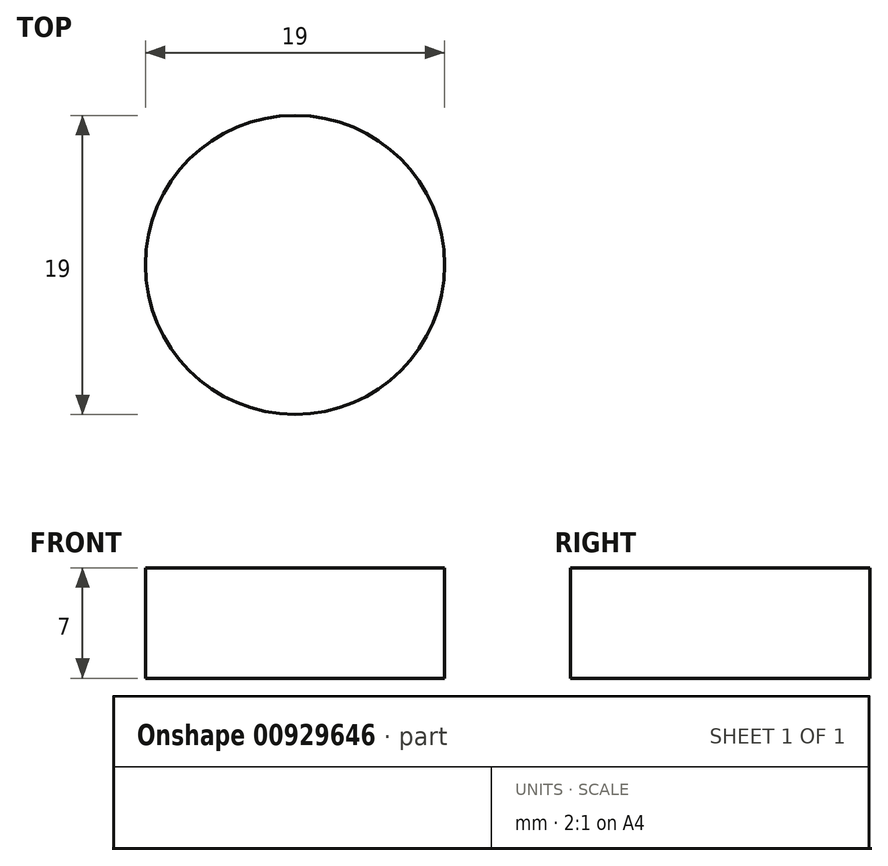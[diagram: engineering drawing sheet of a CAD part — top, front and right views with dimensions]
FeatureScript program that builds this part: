
annotation { "Feature Type Name" : "Feature", "Feature Type Description" : "" }
export const myFeature = defineFeature(function(context is Context, id is Id, definition is map)
    precondition{}
    {
        {
            var Q0;
            Q0=qCreatedBy(makeId("Top.planeOp"),FACE);
            var sketch = newSketch(context, id + "F0", { "sketchPlane" : qUnion([Q0])});
            skLineSegment(sketch, "E0.bottom", {"start": v(-40, 15) * mm, "end": v(40, 15) * mm});
            skLineSegment(sketch, "E0.top", {"start": v(-40, -15) * mm, "end": v(40, -15) * mm});
            skLineSegment(sketch, "E0.left", {"start": v(-40, 15) * mm, "end": v(-40, -15) * mm});
            skLineSegment(sketch, "E0.right", {"start": v(40, 15) * mm, "end": v(40, -15) * mm});
            skPoint(sketch, "E0.middle", {"position": v(0, 0) * mm});
            skSolve(sketch);
        }
        {
            var Q0;
            Q0 = qSketchRegion(id + "F0", true);
            extrude(context, id + "F1", {"entities" : qUnion([Q0]), "depth" : 7 * mm, "offsetDistance" : 25 * mm});
        }
        {
            var Q0;
            Q0=makeQuery(id+"F1.opExtrude","CAP_FACE",FACE,{"disambiguationData":[OSD([sQuery(id+"F0.wireOp",EDGE,"E0.bottom"),sQuery(id+"F0.wireOp",EDGE,"E0.top"),sQuery(id+"F0.wireOp",EDGE,"E0.left"),sQuery(id+"F0.wireOp",EDGE,"E0.right")])],"isStart":false});
            var sketch = newSketch(context, id + "F2", { "sketchPlane" : qUnion([Q0])});
            skCircle(sketch, "E1", {"center": v(0, 0) * mm, "radius": 11 * mm});
            skSolve(sketch);
        }
        {
            var Q0;
            Q0=makeQuery(id+"F2.imprint","IMPRINT",FACE,{"disambiguationData":[TD([[makeQuery(id+"F2.imprint","IMPRINT",EDGE,{"derivedFrom":sQuery(id+"F2.wireOp",EDGE,"E1")}),1.0]])]});
            extrude(context, id + "F3", {"entities" : qUnion([Q0]), "operationType" : NewBodyOperationType.REMOVE, "endBound" : BoundingType.THROUGH_ALL, "oppositeDirection" : true, "depth" : 25 * mm, "offsetDistance" : 25 * mm});
        }
        {
            var Q0;
            Q0=makeQuery(id+"F1.opExtrude","SWEPT_EDGE",EDGE,{"disambiguationData":[OSD([sQuery(id+"F0.wireOp",EDGE,"E0.bottom"),sQuery(id+"F0.wireOp",EDGE,"E0.left")])]});
            var Q1;
            Q1=makeQuery(id+"F1.opExtrude","SWEPT_EDGE",EDGE,{"disambiguationData":[OSD([sQuery(id+"F0.wireOp",EDGE,"E0.top"),sQuery(id+"F0.wireOp",EDGE,"E0.right")])]});
            var Q2;
            Q2=makeQuery(id+"F1.opExtrude","SWEPT_EDGE",EDGE,{"disambiguationData":[OSD([sQuery(id+"F0.wireOp",EDGE,"E0.bottom"),sQuery(id+"F0.wireOp",EDGE,"E0.right")])]});
            var Q3;
            Q3=makeQuery(id+"F1.opExtrude","SWEPT_EDGE",EDGE,{"disambiguationData":[OSD([sQuery(id+"F0.wireOp",EDGE,"E0.top"),sQuery(id+"F0.wireOp",EDGE,"E0.left")])]});
            chamfer(context, id + "F4", {"entities" : qUnion([Q0, Q1, Q2, Q3]), "width" : 10 * mm, "tangentPropagation" : true});
        }
        {
            var Q0;
            {var subQ0=sQuery(id+"F0.wireOp",EDGE,"E0.bottom");Q0=makeQuery(id+"F4.opChamfer","BLEND_EDGE",EDGE,{"blendedFrom":[makeQuery(id+"F1.opExtrude","SWEPT_EDGE",EDGE,{"disambiguationData":[OSD([subQ0,sQuery(id+"F0.wireOp",EDGE,"E0.left")])]}),makeQuery(id+"F1.opExtrude","SWEPT_FACE",FACE,{"disambiguationData":[OSD([subQ0])]})],"blendedInto":[makeQuery(id+"F1.opExtrude","SWEPT_FACE",FACE,{"disambiguationData":[OSD([subQ0])]})]});}
            var Q1;
            {var subQ0=sQuery(id+"F0.wireOp",EDGE,"E0.top");Q1=makeQuery(id+"F4.opChamfer","BLEND_EDGE",EDGE,{"blendedFrom":[makeQuery(id+"F1.opExtrude","SWEPT_EDGE",EDGE,{"disambiguationData":[OSD([subQ0,sQuery(id+"F0.wireOp",EDGE,"E0.left")])]}),makeQuery(id+"F1.opExtrude","SWEPT_FACE",FACE,{"disambiguationData":[OSD([subQ0])]})],"blendedInto":[makeQuery(id+"F1.opExtrude","SWEPT_FACE",FACE,{"disambiguationData":[OSD([subQ0])]})]});}
            var Q2;
            {var subQ0=sQuery(id+"F0.wireOp",EDGE,"E0.top");Q2=makeQuery(id+"F4.opChamfer","BLEND_EDGE",EDGE,{"blendedFrom":[makeQuery(id+"F1.opExtrude","SWEPT_EDGE",EDGE,{"disambiguationData":[OSD([subQ0,sQuery(id+"F0.wireOp",EDGE,"E0.right")])]}),makeQuery(id+"F1.opExtrude","SWEPT_FACE",FACE,{"disambiguationData":[OSD([subQ0])]})],"blendedInto":[makeQuery(id+"F1.opExtrude","SWEPT_FACE",FACE,{"disambiguationData":[OSD([subQ0])]})]});}
            var Q3;
            {var subQ0=sQuery(id+"F0.wireOp",EDGE,"E0.bottom");Q3=makeQuery(id+"F4.opChamfer","BLEND_EDGE",EDGE,{"blendedFrom":[makeQuery(id+"F1.opExtrude","SWEPT_EDGE",EDGE,{"disambiguationData":[OSD([subQ0,sQuery(id+"F0.wireOp",EDGE,"E0.right")])]}),makeQuery(id+"F1.opExtrude","SWEPT_FACE",FACE,{"disambiguationData":[OSD([subQ0])]})],"blendedInto":[makeQuery(id+"F1.opExtrude","SWEPT_FACE",FACE,{"disambiguationData":[OSD([subQ0])]})]});}
            fillet(context, id + "F5", {"entities" : qUnion([Q0, Q1, Q2, Q3]), "radius" : 5 * mm, "tangentPropagation" : true, "allowEdgeOverflow" : false});
        }
        {
            var Q0;
            Q0=makeQuery(id+"F1.opExtrude","CAP_FACE",FACE,{"disambiguationData":[OSD([sQuery(id+"F0.wireOp",EDGE,"E0.bottom"),sQuery(id+"F0.wireOp",EDGE,"E0.top"),sQuery(id+"F0.wireOp",EDGE,"E0.left"),sQuery(id+"F0.wireOp",EDGE,"E0.right")])],"isStart":false});
            var sketch = newSketch(context, id + "F6", { "sketchPlane" : qUnion([Q0])});
            skLineSegment(sketch, "E2", {"start": v(-29.84, 14.62) * mm, "end": v(-29.84, 0) * mm, "construction": true});
            skCircle(sketch, "E3", {"center": v(-29.84, 0) * mm, "radius": 9.5 * mm});
            skLineSegment(sketch, "E4", {"start": v(0, 15) * mm, "end": v(0, -15) * mm, "construction": true});
            skCircle(sketch, "E5.MirrorC", {"center": v(29.84, 0) * mm, "radius": 9.5 * mm});
            skSolve(sketch);
        }
        {
            var Q0;
            Q0=makeQuery(id+"F6.imprint","IMPRINT",FACE,{"disambiguationData":[TD([[makeQuery(id+"F6.imprint","IMPRINT",EDGE,{"derivedFrom":sQuery(id+"F6.wireOp",EDGE,"E5.MirrorC")}),-1.0]])]});
            var Q1;
            Q1=makeQuery(id+"F6.imprint","IMPRINT",FACE,{"disambiguationData":[TD([[makeQuery(id+"F6.imprint","IMPRINT",EDGE,{"derivedFrom":sQuery(id+"F6.wireOp",EDGE,"E3")}),1.0]])]});
            extrude(context, id + "F7", {"entities" : qUnion([Q0, Q1]), "operationType" : NewBodyOperationType.REMOVE, "endBound" : BoundingType.THROUGH_ALL, "oppositeDirection" : true, "depth" : 25 * mm, "offsetDistance" : 25 * mm});
        }
        {
            var Q0;
            Q0=makeQuery(id+"F1.opExtrude","CAP_FACE",FACE,{"disambiguationData":[OSD([sQuery(id+"F0.wireOp",EDGE,"E0.bottom"),sQuery(id+"F0.wireOp",EDGE,"E0.top"),sQuery(id+"F0.wireOp",EDGE,"E0.left"),sQuery(id+"F0.wireOp",EDGE,"E0.right")])],"isStart":false});
            var sketch = newSketch(context, id + "F8", { "sketchPlane" : qUnion([Q0])});
            skLineSegment(sketch, "E6", {"start": v(-17.7, 15) * mm, "end": v(-17.7, -15) * mm});
            skLineSegment(sketch, "E7", {"start": v(-17.7, -15) * mm, "end": v(-15.7, -15) * mm});
            skLineSegment(sketch, "E8", {"start": v(-15.7, -15) * mm, "end": v(-15.7, 15) * mm});
            skLineSegment(sketch, "E9", {"start": v(-15.7, 15) * mm, "end": v(-17.7, 15) * mm});
            skLineSegment(sketch, "E10", {"start": v(0, 15) * mm, "end": v(0, -15) * mm, "construction": true});
            skLineSegment(sketch, "E11.MirrorCS", {"start": v(15.7, -15) * mm, "end": v(15.7, 15) * mm});
            skLineSegment(sketch, "E12.MirrorCS", {"start": v(17.7, 15) * mm, "end": v(17.7, -15) * mm});
            skLineSegment(sketch, "E13.MirrorCS", {"start": v(17.7, -15) * mm, "end": v(15.7, -15) * mm});
            skLineSegment(sketch, "E14.MirrorCS", {"start": v(15.7, 15) * mm, "end": v(17.7, 15) * mm});
            skSolve(sketch);
        }
        {
            var Q0;
            Q0=makeQuery(id+"F8.imprint","IMPRINT",FACE,{"disambiguationData":[TD([[makeQuery(id+"F8.imprint","IMPRINT",EDGE,{"derivedFrom":sQuery(id+"F8.wireOp",EDGE,"E11.MirrorCS")}),-1.0]])]});
            var Q1;
            Q1=makeQuery(id+"F8.imprint","IMPRINT",FACE,{"disambiguationData":[TD([[makeQuery(id+"F8.imprint","IMPRINT",EDGE,{"derivedFrom":sQuery(id+"F8.wireOp",EDGE,"E6")}),1.0]])]});
            extrude(context, id + "F9", {"entities" : qUnion([Q0, Q1]), "operationType" : NewBodyOperationType.REMOVE, "oppositeDirection" : true, "depth" : 2 * mm, "offsetDistance" : 25 * mm});
        }
        {
            var Q0;
            Q0=makeQuery(id+"F1.opExtrude","CAP_FACE",FACE,{"disambiguationData":[OSD([sQuery(id+"F0.wireOp",EDGE,"E0.bottom"),sQuery(id+"F0.wireOp",EDGE,"E0.top"),sQuery(id+"F0.wireOp",EDGE,"E0.left"),sQuery(id+"F0.wireOp",EDGE,"E0.right")])],"isStart":true});
            var sketch = newSketch(context, id + "F10", { "sketchPlane" : qUnion([Q0])});
            skLineSegment(sketch, "E15", {"start": v(-15.68, 15) * mm, "end": v(-15.68, -15) * mm});
            skLineSegment(sketch, "E16", {"start": v(-15.68, -15) * mm, "end": v(-17.68, -15) * mm});
            skLineSegment(sketch, "E17", {"start": v(-17.68, -15) * mm, "end": v(-17.68, 15) * mm});
            skLineSegment(sketch, "E18", {"start": v(-17.68, 15) * mm, "end": v(-15.68, 15) * mm});
            skLineSegment(sketch, "E19", {"start": v(0, 15) * mm, "end": v(0, -15) * mm, "construction": true});
            skLineSegment(sketch, "E20.MirrorCS", {"start": v(15.68, 15) * mm, "end": v(15.68, -15) * mm});
            skLineSegment(sketch, "E21.MirrorCS", {"start": v(17.68, -15) * mm, "end": v(17.68, 15) * mm});
            skLineSegment(sketch, "E22.MirrorCS", {"start": v(17.68, 15) * mm, "end": v(15.68, 15) * mm});
            skLineSegment(sketch, "E23.MirrorCS", {"start": v(15.68, -15) * mm, "end": v(17.68, -15) * mm});
            skSolve(sketch);
        }
        {
            var Q0;
            Q0=makeQuery(id+"F10.imprint","IMPRINT",FACE,{"disambiguationData":[TD([[makeQuery(id+"F10.imprint","IMPRINT",EDGE,{"derivedFrom":sQuery(id+"F10.wireOp",EDGE,"E20.MirrorCS")}),1.0]])]});
            var Q1;
            Q1=makeQuery(id+"F10.imprint","IMPRINT",FACE,{"disambiguationData":[TD([[makeQuery(id+"F10.imprint","IMPRINT",EDGE,{"derivedFrom":sQuery(id+"F10.wireOp",EDGE,"E15")}),-1.0]])]});
            extrude(context, id + "F11", {"entities" : qUnion([Q0, Q1]), "operationType" : NewBodyOperationType.REMOVE, "oppositeDirection" : true, "depth" : 2 * mm, "offsetDistance" : 25 * mm});
        }
    });
